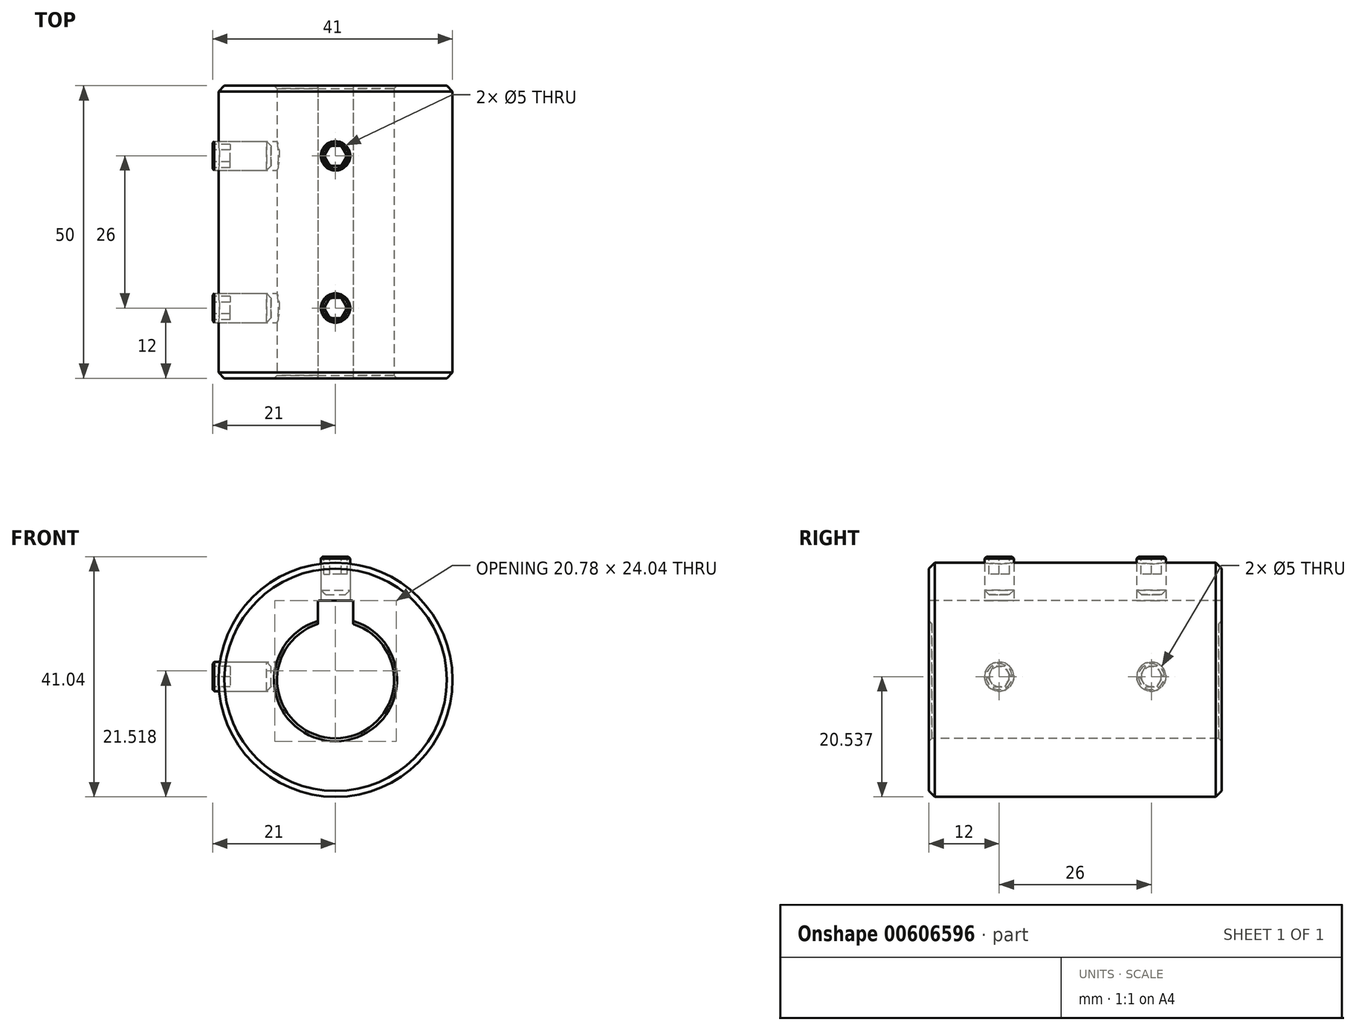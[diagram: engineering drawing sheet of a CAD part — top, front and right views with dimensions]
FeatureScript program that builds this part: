
annotation { "Feature Type Name" : "Feature", "Feature Type Description" : "" }
export const myFeature = defineFeature(function(context is Context, id is Id, definition is map)
    precondition{}
    {
        {
            var Q0;
            Q0=qCreatedBy(makeId("Front.planeOp"),FACE);
            var sketch = newSketch(context, id + "F0", { "sketchPlane" : qUnion([Q0])});
            skCircle(sketch, "E0", {"center": v(-120.11, 70.6) * mm, "radius": 20 * mm});
            skLineSegment(sketch, "E1.bottom", {"start": v(-123.11, 80.15) * mm, "end": v(-123.11, 80.15) * mm});
            skLineSegment(sketch, "E1.top", {"start": v(-122.91, 84.15) * mm, "end": v(-117.31, 84.15) * mm});
            skLineSegment(sketch, "E1.left", {"start": v(-123.11, 80.22) * mm, "end": v(-123.11, 83.95) * mm});
            skLineSegment(sketch, "E1.right", {"start": v(-117.11, 80.3) * mm, "end": v(-117.11, 83.95) * mm});
            skArc(sketch, "E2", {"start": v(-123.18, 80.13) * mm, "mid": v(-120.15, 60.6) * mm, "end": v(-116.97, 80.1) * mm});
            skLineSegment(sketch, "E3", {"start": v(-117.11, 80.15) * mm, "end": v(-117.11, 80.15) * mm});
            skPoint(sketch, "E4.visualSharp", {"position": v(-123.11, 84.15) * mm});
            skArc(sketch, "E4.filletArc", {"start": v(-122.91, 84.15) * mm, "mid": v(-123.05, 84.09) * mm, "end": v(-123.11, 83.95) * mm});
            skPoint(sketch, "E5.visualSharp", {"position": v(-117.11, 84.15) * mm});
            skArc(sketch, "E5.filletArc", {"start": v(-117.11, 83.95) * mm, "mid": v(-117.17, 84.09) * mm, "end": v(-117.31, 84.15) * mm});
            skPoint(sketch, "E6.visualSharp", {"position": v(-123.11, 80.15) * mm});
            skArc(sketch, "E6.filletArc", {"start": v(-123.18, 80.13) * mm, "mid": v(-123.13, 80.16) * mm, "end": v(-123.11, 80.22) * mm});
            skPoint(sketch, "E7.visualSharp", {"position": v(-117.11, 80.15) * mm});
            skArc(sketch, "E7.filletArc", {"start": v(-117.11, 80.3) * mm, "mid": v(-117.07, 80.18) * mm, "end": v(-116.97, 80.1) * mm});
            skSolve(sketch);
        }
        {
            var Q0;
            Q0=makeQuery(id+"F0.imprint","IMPRINT",FACE,{"disambiguationData":[TD([[makeQuery(id+"F0.imprint","IMPRINT",EDGE,{"derivedFrom":sQuery(id+"F0.wireOp",EDGE,"E0")}),1.0]])]});
            extrude(context, id + "F1", {"entities" : qUnion([Q0]), "oppositeDirection" : true, "depth" : 50 * mm, "offsetDistance" : 25 * mm});
        }
        {
            var Q0;
            Q0=makeQuery(id+"F1.opExtrude","CAP_EDGE",EDGE,{"disambiguationData":[OSD([sQuery(id+"F0.wireOp",EDGE,"E0")])],"isStart":true});
            var Q1;
            Q1=makeQuery(id+"F1.opExtrude","CAP_EDGE",EDGE,{"disambiguationData":[OSD([sQuery(id+"F0.wireOp",EDGE,"E0")])],"isStart":false});
            chamfer(context, id + "F2", {"entities" : qUnion([Q0, Q1]), "width" : 1 * mm, "tangentPropagation" : true});
        }
        {
            var Q0;
            Q0=makeQuery(id+"F1.opExtrude","SWEPT_FACE",FACE,{"disambiguationData":[OSD([sQuery(id+"F0.wireOp",EDGE,"E1.top")])]});
            var sketch = newSketch(context, id + "F3", { "sketchPlane" : qUnion([Q0])});
            skCircle(sketch, "E8", {"center": v(-120.11, -12) * mm, "radius": 2.5 * mm});
            skCircle(sketch, "E9", {"center": v(-120.11, -38) * mm, "radius": 2.5 * mm});
            skLineSegment(sketch, "E10", {"start": v(-120.11, -38) * mm, "end": v(-120.11, -50) * mm, "construction": true});
            skLineSegment(sketch, "E11", {"start": v(-117.31, -25) * mm, "end": v(-122.91, -25) * mm, "construction": true});
            skSolve(sketch);
        }
        {
            var Q0;
            Q0=makeQuery(id+"F3.imprint","IMPRINT",FACE,{"disambiguationData":[TD([[makeQuery(id+"F3.imprint","IMPRINT",EDGE,{"derivedFrom":sQuery(id+"F3.wireOp",EDGE,"E8")}),1.0]])]});
            var Q1;
            {var subQ0=sQuery(id+"F3.wireOp",EDGE,"E9");var subQ1=makeQuery(id+"F1.opExtrude","SWEPT_EDGE",EDGE,{"disambiguationData":[OSD([sQuery(id+"F0.wireOp",EDGE,"E1.top"),sQuery(id+"F0.wireOp",EDGE,"E5.filletArc")])]});var subQ2=makeQuery(id+"F3.imprint","INTERSECT",VERTEX,{"disambiguationData":[OD(0.0)],"derivedFrom":[subQ1,subQ0]});Q1=makeQuery(id+"F3.imprint","IMPRINT",FACE,{"disambiguationData":[TD([[makeQuery(id+"F3.imprint","IMPRINT",EDGE,{"disambiguationData":[TD([[subQ2,-1.0]])],"derivedFrom":subQ0}),1.0]])]});}
            extrude(context, id + "F4", {"entities" : qUnion([Q0, Q1]), "operationType" : NewBodyOperationType.REMOVE, "endBound" : BoundingType.THROUGH_ALL, "oppositeDirection" : true, "depth" : 25 * mm, "offsetDistance" : 25 * mm});
        }
        {
            var Q0;
            Q0=makeQuery(id+"F1.opExtrude","SWEPT_FACE",FACE,{"disambiguationData":[OSD([sQuery(id+"F0.wireOp",EDGE,"E1.left")])]});
            cPlane(context, id + "F5", {"entities" : qUnion([Q0]), "cplaneType" : CPlaneType.OFFSET, "offset" : 3 * mm, "width" : 150 * mm, "height" : 150 * mm});
        }
        {
            var Q0;
            Q0=qCreatedBy(id+"F5.planeOp",FACE);
            var sketch = newSketch(context, id + "F6", { "sketchPlane" : qUnion([Q0])});
            skCircle(sketch, "E12", {"center": v(12, 71.15) * mm, "radius": 2.5 * mm});
            skCircle(sketch, "E13", {"center": v(38, 71.15) * mm, "radius": 2.5 * mm});
            skSolve(sketch);
        }
        {
            var Q0;
            Q0=makeQuery(id+"F6.imprint","IMPRINT",FACE,{"disambiguationData":[TD([[makeQuery(id+"F6.imprint","IMPRINT",EDGE,{"derivedFrom":sQuery(id+"F6.wireOp",EDGE,"E12")}),1.0]])]});
            var Q1;
            Q1=makeQuery(id+"F6.imprint","IMPRINT",FACE,{"disambiguationData":[TD([[makeQuery(id+"F6.imprint","IMPRINT",EDGE,{"derivedFrom":sQuery(id+"F6.wireOp",EDGE,"E13")}),1.0]])]});
            extrude(context, id + "F7", {"entities" : qUnion([Q0, Q1]), "operationType" : NewBodyOperationType.REMOVE, "endBound" : BoundingType.THROUGH_ALL, "oppositeDirection" : true, "depth" : 25 * mm, "offsetDistance" : 25 * mm});
        }
        {
            var Q0;
            Q0=makeQuery(id+"F6.imprint","IMPRINT",FACE,{"disambiguationData":[TD([[makeQuery(id+"F6.imprint","IMPRINT",EDGE,{"derivedFrom":sQuery(id+"F6.wireOp",EDGE,"E13")}),1.0]])]});
            var Q1;
            Q1=makeQuery(id+"F6.imprint","IMPRINT",FACE,{"disambiguationData":[TD([[makeQuery(id+"F6.imprint","IMPRINT",EDGE,{"derivedFrom":sQuery(id+"F6.wireOp",EDGE,"E12")}),1.0]])]});
            var Q2;
            Q2=sQuery(id+"F6.wireOp",EDGE,"E13");
            var Q3;
            Q3=sQuery(id+"F6.wireOp",EDGE,"E12");
            extrude(context, id + "F8", {"entities" : qUnion([Q0, Q1]), "surfaceEntities" : qUnion([Q2, Q3]), "oppositeDirection" : true, "depth" : 21 * mm, "offsetDistance" : 25 * mm, "hasSecondDirection" : true, "secondDirectionOppositeDirection" : false, "secondDirectionDepth" : -11 * mm});
        }
        {
            var Q0;
            Q0=makeQuery(id+"F3.imprint","IMPRINT",FACE,{"disambiguationData":[TD([[makeQuery(id+"F3.imprint","IMPRINT",EDGE,{"derivedFrom":sQuery(id+"F3.wireOp",EDGE,"E9")}),1.0]])]});
            var Q1;
            Q1=makeQuery(id+"F3.imprint","IMPRINT",FACE,{"disambiguationData":[TD([[makeQuery(id+"F3.imprint","IMPRINT",EDGE,{"derivedFrom":sQuery(id+"F3.wireOp",EDGE,"E8")}),1.0]])]});
            extrude(context, id + "F9", {"entities" : qUnion([Q0, Q1]), "oppositeDirection" : true, "depth" : 7.5 * mm, "offsetDistance" : 25 * mm, "hasSecondDirection" : true, "secondDirectionOppositeDirection" : false, "secondDirectionDepth" : -1 * mm});
        }
        {
            var Q0;
            Q0=makeQuery(id+"F8.opExtrude","CAP_EDGE",EDGE,{"disambiguationData":[OSD([sQuery(id+"F6.wireOp",EDGE,"E13")])],"isStart":true});
            var Q1;
            Q1=makeQuery(id+"F8.opExtrude","CAP_EDGE",EDGE,{"disambiguationData":[OSD([sQuery(id+"F6.wireOp",EDGE,"E12")])],"isStart":true});
            var Q2;
            Q2=makeQuery(id+"F9.opExtrude","CAP_EDGE",EDGE,{"disambiguationData":[OSD([sQuery(id+"F3.wireOp",EDGE,"E8")])],"isStart":true});
            var Q3;
            Q3=makeQuery(id+"F9.opExtrude","CAP_EDGE",EDGE,{"disambiguationData":[OSD([sQuery(id+"F3.wireOp",EDGE,"E9")])],"isStart":true});
            chamfer(context, id + "F10", {"entities" : qUnion([Q0, Q1, Q2, Q3]), "width" : 0.8 * mm, "tangentPropagation" : true});
        }
        {
            var Q0;
            Q0=makeQuery(id+"F9.opExtrude","CAP_FACE",FACE,{"disambiguationData":[OSD([sQuery(id+"F3.wireOp",EDGE,"E9")])],"isStart":false});
            var sketch = newSketch(context, id + "F11", { "sketchPlane" : qUnion([Q0])});
            skCircle(sketch, "E14.cCircle", {"center": v(-120.11, 38) * mm, "radius": 2 * mm, "construction": true});
            skLineSegment(sketch, "E14.0", {"start": v(-119.11, 36.27) * mm, "end": v(-121.11, 36.27) * mm});
            skLineSegment(sketch, "E14.1", {"start": v(-121.11, 36.27) * mm, "end": v(-122.11, 38) * mm});
            skLineSegment(sketch, "E14.2", {"start": v(-122.11, 38) * mm, "end": v(-121.11, 39.73) * mm});
            skLineSegment(sketch, "E14.3", {"start": v(-121.11, 39.73) * mm, "end": v(-119.11, 39.73) * mm});
            skLineSegment(sketch, "E14.4", {"start": v(-119.11, 39.73) * mm, "end": v(-118.11, 38) * mm});
            skLineSegment(sketch, "E14.5", {"start": v(-118.11, 38) * mm, "end": v(-119.11, 36.27) * mm});
            skCircle(sketch, "E15.cCircle", {"center": v(-120.11, 12) * mm, "radius": 2 * mm, "construction": true});
            skLineSegment(sketch, "E15.0", {"start": v(-119.11, 10.27) * mm, "end": v(-121.11, 10.27) * mm});
            skLineSegment(sketch, "E15.1", {"start": v(-121.11, 10.27) * mm, "end": v(-122.11, 12) * mm});
            skLineSegment(sketch, "E15.2", {"start": v(-122.11, 12) * mm, "end": v(-121.11, 13.73) * mm});
            skLineSegment(sketch, "E15.3", {"start": v(-121.11, 13.73) * mm, "end": v(-119.11, 13.73) * mm});
            skLineSegment(sketch, "E15.4", {"start": v(-119.11, 13.73) * mm, "end": v(-118.11, 12) * mm});
            skLineSegment(sketch, "E15.5", {"start": v(-118.11, 12) * mm, "end": v(-119.11, 10.27) * mm});
            skSolve(sketch);
        }
        {
            var Q0;
            Q0=qSketchRegion(id+"F11",true);
            extrude(context, id + "F12", {"entities" : qUnion([Q0]), "operationType" : NewBodyOperationType.REMOVE, "oppositeDirection" : true, "depth" : 3 * mm, "offsetDistance" : 25 * mm});
        }
        {
            var Q0;
            Q0=makeQuery(id+"F9.opExtrude","CAP_EDGE",EDGE,{"disambiguationData":[OSD([sQuery(id+"F3.wireOp",EDGE,"E9")])],"isStart":false});
            var Q1;
            Q1=makeQuery(id+"F9.opExtrude","CAP_EDGE",EDGE,{"disambiguationData":[OSD([sQuery(id+"F3.wireOp",EDGE,"E8")])],"isStart":false});
            var Q2;
            Q2=makeQuery(id+"F8.opExtrude","CAP_EDGE",EDGE,{"disambiguationData":[OSD([sQuery(id+"F6.wireOp",EDGE,"E13")])],"isStart":false});
            var Q3;
            Q3=makeQuery(id+"F8.opExtrude","CAP_EDGE",EDGE,{"disambiguationData":[OSD([sQuery(id+"F6.wireOp",EDGE,"E12")])],"isStart":false});
            chamfer(context, id + "F13", {"entities" : qUnion([Q0, Q1, Q2, Q3]), "width" : 0.3 * mm, "tangentPropagation" : true});
        }
        {
            var Q0;
            Q0=makeQuery(id+"F8.opExtrude","CAP_FACE",FACE,{"disambiguationData":[OSD([sQuery(id+"F6.wireOp",EDGE,"E13")])],"isStart":false});
            var sketch = newSketch(context, id + "F14", { "sketchPlane" : qUnion([Q0])});
            skCircle(sketch, "E16.cCircle", {"center": v(-38, 71.15) * mm, "radius": 2 * mm, "construction": true});
            skLineSegment(sketch, "E16.0", {"start": v(-37, 69.42) * mm, "end": v(-39, 69.42) * mm});
            skLineSegment(sketch, "E16.1", {"start": v(-39, 69.42) * mm, "end": v(-40, 71.15) * mm});
            skLineSegment(sketch, "E16.2", {"start": v(-40, 71.15) * mm, "end": v(-39, 72.88) * mm});
            skLineSegment(sketch, "E16.3", {"start": v(-39, 72.88) * mm, "end": v(-37, 72.88) * mm});
            skLineSegment(sketch, "E16.4", {"start": v(-37, 72.88) * mm, "end": v(-36, 71.15) * mm});
            skLineSegment(sketch, "E16.5", {"start": v(-36, 71.15) * mm, "end": v(-37, 69.42) * mm});
            skCircle(sketch, "E17.cCircle", {"center": v(-12, 71.15) * mm, "radius": 2 * mm, "construction": true});
            skLineSegment(sketch, "E17.0", {"start": v(-11, 69.42) * mm, "end": v(-13, 69.42) * mm});
            skLineSegment(sketch, "E17.1", {"start": v(-13, 69.42) * mm, "end": v(-14, 71.15) * mm});
            skLineSegment(sketch, "E17.2", {"start": v(-14, 71.15) * mm, "end": v(-13, 72.88) * mm});
            skLineSegment(sketch, "E17.3", {"start": v(-13, 72.88) * mm, "end": v(-11, 72.88) * mm});
            skLineSegment(sketch, "E17.4", {"start": v(-11, 72.88) * mm, "end": v(-10, 71.15) * mm});
            skLineSegment(sketch, "E17.5", {"start": v(-10, 71.15) * mm, "end": v(-11, 69.42) * mm});
            skSolve(sketch);
        }
        {
            var Q0;
            Q0=qSketchRegion(id+"F14",true);
            extrude(context, id + "F15", {"entities" : qUnion([Q0]), "operationType" : NewBodyOperationType.REMOVE, "oppositeDirection" : true, "depth" : 3 * mm, "offsetDistance" : 25 * mm});
        }
        {
            var Q0;
            Q0=makeQuery(id+"F1.opExtrude","CAP_EDGE",EDGE,{"disambiguationData":[OSD([sQuery(id+"F0.wireOp",EDGE,"E2")])],"isStart":true});
            var Q1;
            Q1=makeQuery(id+"F1.opExtrude","CAP_EDGE",EDGE,{"disambiguationData":[OSD([sQuery(id+"F0.wireOp",EDGE,"E2")])],"isStart":false});
            chamfer(context, id + "F16", {"entities" : qUnion([Q0, Q1]), "width" : 0.5 * mm});
        }
    });
